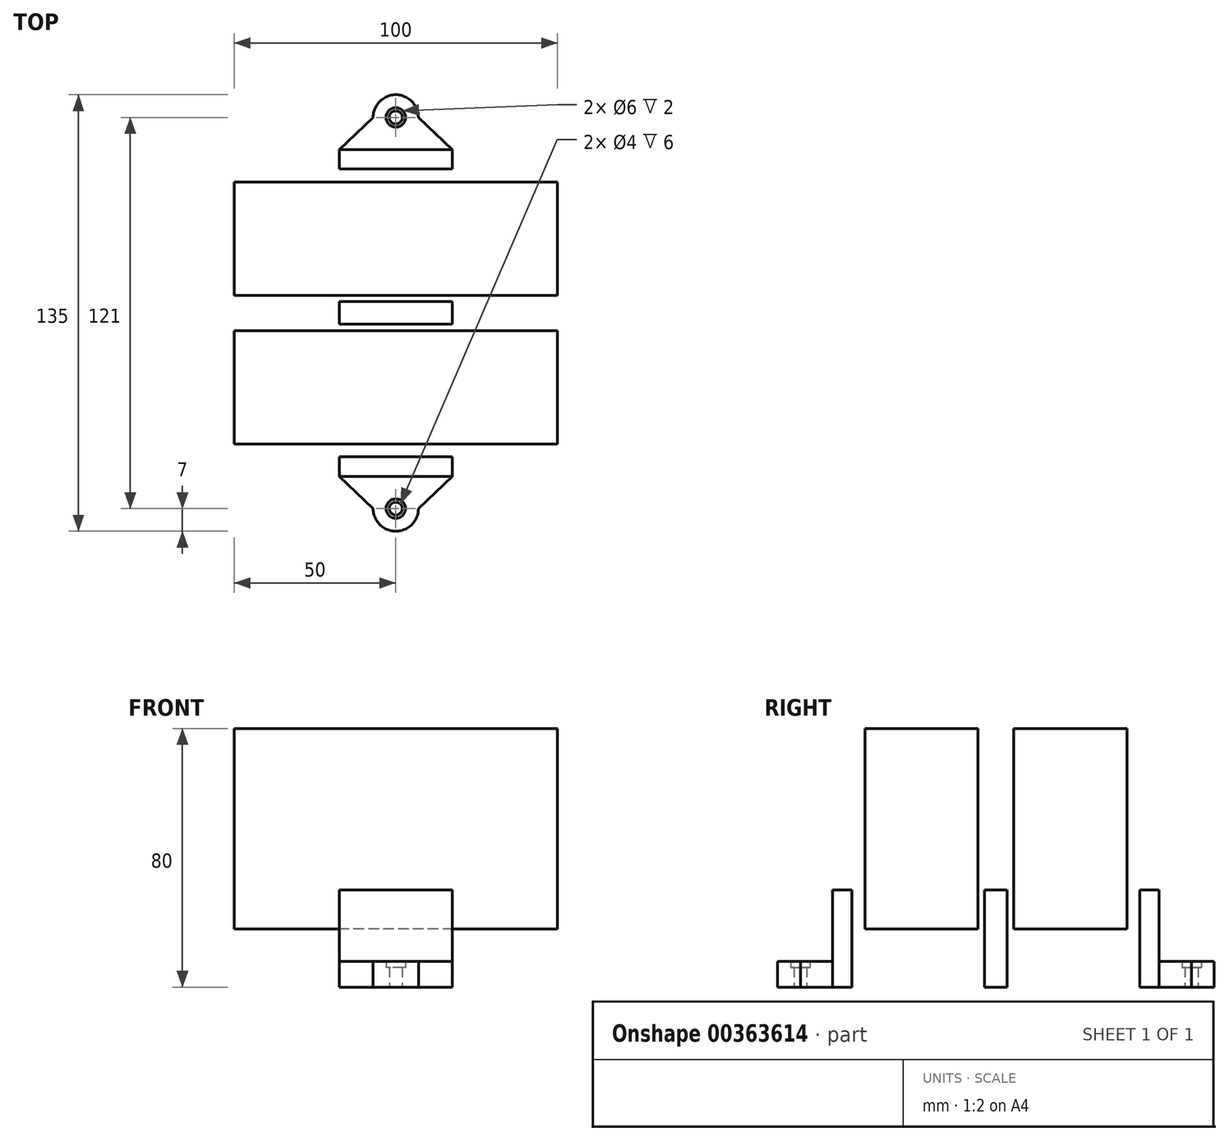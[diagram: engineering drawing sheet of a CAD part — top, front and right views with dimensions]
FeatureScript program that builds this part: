
annotation { "Feature Type Name" : "Feature", "Feature Type Description" : "" }
export const myFeature = defineFeature(function(context is Context, id is Id, definition is map)
    precondition{}
    {
        {
            assignVariable(context, id + "F0", {"name" : "door_hover", "anyValue" : 18});
        }
        {
            assignVariable(context, id + "F1", {"name" : "guide_height", "anyValue" : 30});
        }
        {
            var Q0;
            Q0=qCreatedBy(makeId("Top.planeOp"),FACE);
            var sketch = newSketch(context, id + "F2", { "sketchPlane" : qUnion([Q0])});
            skLineSegment(sketch, "E0", {"start": v(0, 5.5) * mm, "end": v(0, -5.5) * mm, "construction": true});
            skLineSegment(sketch, "E1.bottom", {"start": v(50, 5.5) * mm, "end": v(-50, 5.5) * mm});
            skLineSegment(sketch, "E1.top", {"start": v(50, 40.5) * mm, "end": v(-50, 40.5) * mm});
            skLineSegment(sketch, "E1.left", {"start": v(50, 5.5) * mm, "end": v(50, 40.5) * mm});
            skLineSegment(sketch, "E1.right", {"start": v(-50, 5.5) * mm, "end": v(-50, 40.5) * mm});
            skLineSegment(sketch, "E2.bottom", {"start": v(50, -40.5) * mm, "end": v(-50, -40.5) * mm});
            skLineSegment(sketch, "E2.top", {"start": v(50, -5.5) * mm, "end": v(-50, -5.5) * mm});
            skLineSegment(sketch, "E2.left", {"start": v(50, -40.5) * mm, "end": v(50, -5.5) * mm});
            skLineSegment(sketch, "E2.right", {"start": v(-50, -40.5) * mm, "end": v(-50, -5.5) * mm});
            skSolve(sketch);
        }
        {
            var Q0;
            Q0=makeQuery(id+"F2.imprint","IMPRINT",FACE,{"disambiguationData":[TD([[makeQuery(id+"F2.imprint","IMPRINT",EDGE,{"derivedFrom":sQuery(id+"F2.wireOp",EDGE,"E1.bottom")}),-1.0]])]});
            var Q1;
            Q1=makeQuery(id+"F2.imprint","IMPRINT",FACE,{"disambiguationData":[TD([[makeQuery(id+"F2.imprint","IMPRINT",EDGE,{"derivedFrom":sQuery(id+"F2.wireOp",EDGE,"E2.bottom")}),-1.0]])]});
            extrude(context, id + "F3", {"entities" : qUnion([Q0, Q1]), "depth" : 80 * mm, "hasSecondDirection" : true, "secondDirectionOppositeDirection" : false, "secondDirectionDepth" : (getVariable(context, 'door_hover')) * mm});
        }
        {
            var Q0;
            Q0=qCreatedBy(makeId("Top.planeOp"),FACE);
            var sketch = newSketch(context, id + "F4", { "sketchPlane" : qUnion([Q0])});
            skLineSegment(sketch, "E3.bottom", {"start": v(17.5, -3.5) * mm, "end": v(-17.5, -3.5) * mm});
            skLineSegment(sketch, "E3.top", {"start": v(17.5, 3.5) * mm, "end": v(-17.5, 3.5) * mm});
            skLineSegment(sketch, "E3.left", {"start": v(17.5, -3.5) * mm, "end": v(17.5, 3.5) * mm});
            skLineSegment(sketch, "E3.right", {"start": v(-17.5, -3.5) * mm, "end": v(-17.5, 3.5) * mm});
            skPoint(sketch, "E3.middle", {"position": v(0, 0) * mm});
            skLineSegment(sketch, "E4", {"start": v(0, 0) * mm, "end": v(0, 47.5) * mm, "construction": true});
            skLineSegment(sketch, "E5.bottom", {"start": v(17.5, 44.5) * mm, "end": v(-17.5, 44.5) * mm});
            skLineSegment(sketch, "E5.top", {"start": v(17.5, 50.5) * mm, "end": v(-17.5, 50.5) * mm});
            skLineSegment(sketch, "E5.left", {"start": v(17.5, 44.5) * mm, "end": v(17.5, 50.5) * mm});
            skLineSegment(sketch, "E5.right", {"start": v(-17.5, 44.5) * mm, "end": v(-17.5, 50.5) * mm});
            skPoint(sketch, "E5.middle", {"position": v(0, 47.5) * mm});
            skLineSegment(sketch, "E6", {"start": v(0, 0) * mm, "end": v(0, -47.5) * mm, "construction": true});
            skLineSegment(sketch, "E7.bottom", {"start": v(17.5, -50.5) * mm, "end": v(-17.5, -50.5) * mm});
            skLineSegment(sketch, "E7.top", {"start": v(17.5, -44.5) * mm, "end": v(-17.5, -44.5) * mm});
            skLineSegment(sketch, "E7.left", {"start": v(17.5, -50.5) * mm, "end": v(17.5, -44.5) * mm});
            skLineSegment(sketch, "E7.right", {"start": v(-17.5, -50.5) * mm, "end": v(-17.5, -44.5) * mm});
            skPoint(sketch, "E7.middle", {"position": v(0, -47.5) * mm});
            skLineSegment(sketch, "E8", {"start": v(0, 47.5) * mm, "end": v(0, 60.5) * mm, "construction": true});
            skLineSegment(sketch, "E9", {"start": v(0, -47.5) * mm, "end": v(0, -60.5) * mm, "construction": true});
            skCircle(sketch, "E10", {"center": v(0, 60.5) * mm, "radius": 3 * mm});
            skCircle(sketch, "E11", {"center": v(0, 60.5) * mm, "radius": 2 * mm});
            skCircle(sketch, "E12.0", {"center": v(0, 60.5) * mm, "radius": 7 * mm});
            skCircle(sketch, "E13", {"center": v(0, -60.5) * mm, "radius": 2 * mm});
            skCircle(sketch, "E14", {"center": v(0, -60.5) * mm, "radius": 3 * mm});
            skCircle(sketch, "E15", {"center": v(0, -60.5) * mm, "radius": 7 * mm});
            skLineSegment(sketch, "E16", {"start": v(-7, 60.48) * mm, "end": v(-17.5, 50.5) * mm});
            skLineSegment(sketch, "E17", {"start": v(7, 60.48) * mm, "end": v(17.5, 50.5) * mm});
            skLineSegment(sketch, "E18", {"start": v(7, -60.48) * mm, "end": v(17.5, -50.5) * mm});
            skLineSegment(sketch, "E19", {"start": v(-7, -60.48) * mm, "end": v(-17.5, -50.5) * mm});
            skLineSegment(sketch, "E20.bottom", {"start": v(11.7, -44.5) * mm, "end": v(-11.7, -44.5) * mm});
            skLineSegment(sketch, "E20.top", {"start": v(11.7, 44.5) * mm, "end": v(-11.7, 44.5) * mm});
            skLineSegment(sketch, "E20.left", {"start": v(11.7, -44.5) * mm, "end": v(11.7, 44.5) * mm});
            skLineSegment(sketch, "E20.right", {"start": v(-11.7, -44.5) * mm, "end": v(-11.7, 44.5) * mm});
            skSolve(sketch);
        }
        {
            var Q0;
            Q0=makeQuery(id+"F4.imprint","IMPRINT",FACE,{"disambiguationData":[TD([[makeQuery(id+"F4.imprint","IMPRINT",EDGE,{"derivedFrom":sQuery(id+"F4.wireOp",EDGE,"E10")}),-1.0]])]});
            var Q1;
            Q1=makeQuery(id+"F4.imprint","IMPRINT",FACE,{"disambiguationData":[TD([[makeQuery(id+"F4.imprint","IMPRINT",EDGE,{"derivedFrom":sQuery(id+"F4.wireOp",EDGE,"E5.top")}),-1.0]])]});
            var Q2;
            Q2=makeQuery(id+"F4.imprint","IMPRINT",FACE,{"disambiguationData":[TD([[makeQuery(id+"F4.imprint","IMPRINT",EDGE,{"derivedFrom":sQuery(id+"F4.wireOp",EDGE,"E5.top")}),1.0]])]});
            var Q3;
            {var subQ5=sQuery(id+"F4.wireOp",EDGE,"E20.top");Q3=makeQuery(id+"F4.imprint","IMPRINT",FACE,{"disambiguationData":[TD([[makeQuery(id+"F4.imprint","IMPRINT",EDGE,{"derivedFrom":subQ5}),1.0]])]});}
            var Q4;
            {var subQ0=sQuery(id+"F4.wireOp",EDGE,"E3.left");Q4=makeQuery(id+"F4.imprint","IMPRINT",FACE,{"disambiguationData":[TD([[makeQuery(id+"F4.imprint","IMPRINT",EDGE,{"derivedFrom":subQ0}),1.0]])]});}
            var Q5;
            {var subQ0=sQuery(id+"F4.wireOp",EDGE,"E20.left");var subQ1=sQuery(id+"F4.wireOp",EDGE,"E3.bottom");var subQ2=makeQuery(id+"F4.imprint","INTERSECT",VERTEX,{"derivedFrom":[subQ1,subQ0]});Q5=makeQuery(id+"F4.imprint","IMPRINT",FACE,{"disambiguationData":[TD([[makeQuery(id+"F4.imprint","IMPRINT",EDGE,{"disambiguationData":[TD([[subQ2,-1.0]])],"derivedFrom":subQ1}),-1.0]])]});}
            var Q6;
            {var subQ0=sQuery(id+"F4.wireOp",EDGE,"E3.right");Q6=makeQuery(id+"F4.imprint","IMPRINT",FACE,{"disambiguationData":[TD([[makeQuery(id+"F4.imprint","IMPRINT",EDGE,{"derivedFrom":subQ0}),-1.0]])]});}
            var Q7;
            {var subQ5=sQuery(id+"F4.wireOp",EDGE,"E20.bottom");Q7=makeQuery(id+"F4.imprint","IMPRINT",FACE,{"disambiguationData":[TD([[makeQuery(id+"F4.imprint","IMPRINT",EDGE,{"derivedFrom":subQ5}),-1.0]])]});}
            var Q8;
            Q8=makeQuery(id+"F4.imprint","IMPRINT",FACE,{"disambiguationData":[TD([[makeQuery(id+"F4.imprint","IMPRINT",EDGE,{"derivedFrom":sQuery(id+"F4.wireOp",EDGE,"E7.bottom")}),-1.0]])]});
            var Q9;
            Q9=makeQuery(id+"F4.imprint","IMPRINT",FACE,{"disambiguationData":[TD([[makeQuery(id+"F4.imprint","IMPRINT",EDGE,{"derivedFrom":sQuery(id+"F4.wireOp",EDGE,"E7.bottom")}),1.0]])]});
            var Q10;
            Q10=makeQuery(id+"F4.imprint","IMPRINT",FACE,{"disambiguationData":[TD([[makeQuery(id+"F4.imprint","IMPRINT",EDGE,{"derivedFrom":sQuery(id+"F4.wireOp",EDGE,"E14")}),-1.0]])]});
            extrude(context, id + "F5", {"entities" : qUnion([Q0, Q1, Q2, Q3, Q4, Q5, Q6, Q7, Q8, Q9, Q10]), "depth" : 8 * mm});
        }
        {
            var Q0;
            {var subQ0=sQuery(id+"F4.wireOp",EDGE,"E3.left");Q0=makeQuery(id+"F4.imprint","IMPRINT",FACE,{"disambiguationData":[TD([[makeQuery(id+"F4.imprint","IMPRINT",EDGE,{"derivedFrom":subQ0}),1.0]])]});}
            var Q1;
            {var subQ0=sQuery(id+"F4.wireOp",EDGE,"E20.left");var subQ1=sQuery(id+"F4.wireOp",EDGE,"E3.bottom");var subQ2=makeQuery(id+"F4.imprint","INTERSECT",VERTEX,{"derivedFrom":[subQ1,subQ0]});Q1=makeQuery(id+"F4.imprint","IMPRINT",FACE,{"disambiguationData":[TD([[makeQuery(id+"F4.imprint","IMPRINT",EDGE,{"disambiguationData":[TD([[subQ2,-1.0]])],"derivedFrom":subQ1}),-1.0]])]});}
            var Q2;
            {var subQ0=sQuery(id+"F4.wireOp",EDGE,"E3.right");Q2=makeQuery(id+"F4.imprint","IMPRINT",FACE,{"disambiguationData":[TD([[makeQuery(id+"F4.imprint","IMPRINT",EDGE,{"derivedFrom":subQ0}),-1.0]])]});}
            var Q3;
            Q3=makeQuery(id+"F4.imprint","IMPRINT",FACE,{"disambiguationData":[TD([[makeQuery(id+"F4.imprint","IMPRINT",EDGE,{"derivedFrom":sQuery(id+"F4.wireOp",EDGE,"E7.bottom")}),-1.0]])]});
            var Q4;
            Q4=makeQuery(id+"F4.imprint","IMPRINT",FACE,{"disambiguationData":[TD([[makeQuery(id+"F4.imprint","IMPRINT",EDGE,{"derivedFrom":sQuery(id+"F4.wireOp",EDGE,"E5.top")}),1.0]])]});
            extrude(context, id + "F6", {"entities" : qUnion([Q0, Q1, Q2, Q3, Q4]), "operationType" : NewBodyOperationType.ADD, "depth" : (getVariable(context, 'guide_height')) * mm});
        }
        {
            var Q0;
            Q0=makeQuery(id+"F4.imprint","IMPRINT",FACE,{"disambiguationData":[TD([[makeQuery(id+"F4.imprint","IMPRINT",EDGE,{"derivedFrom":sQuery(id+"F4.wireOp",EDGE,"E10")}),1.0]])]});
            var Q1;
            Q1=makeQuery(id+"F4.imprint","IMPRINT",FACE,{"disambiguationData":[TD([[makeQuery(id+"F4.imprint","IMPRINT",EDGE,{"derivedFrom":sQuery(id+"F4.wireOp",EDGE,"E13")}),-1.0]])]});
            extrude(context, id + "F7", {"entities" : qUnion([Q0, Q1]), "operationType" : NewBodyOperationType.ADD, "depth" : 6 * mm});
        }
    });
